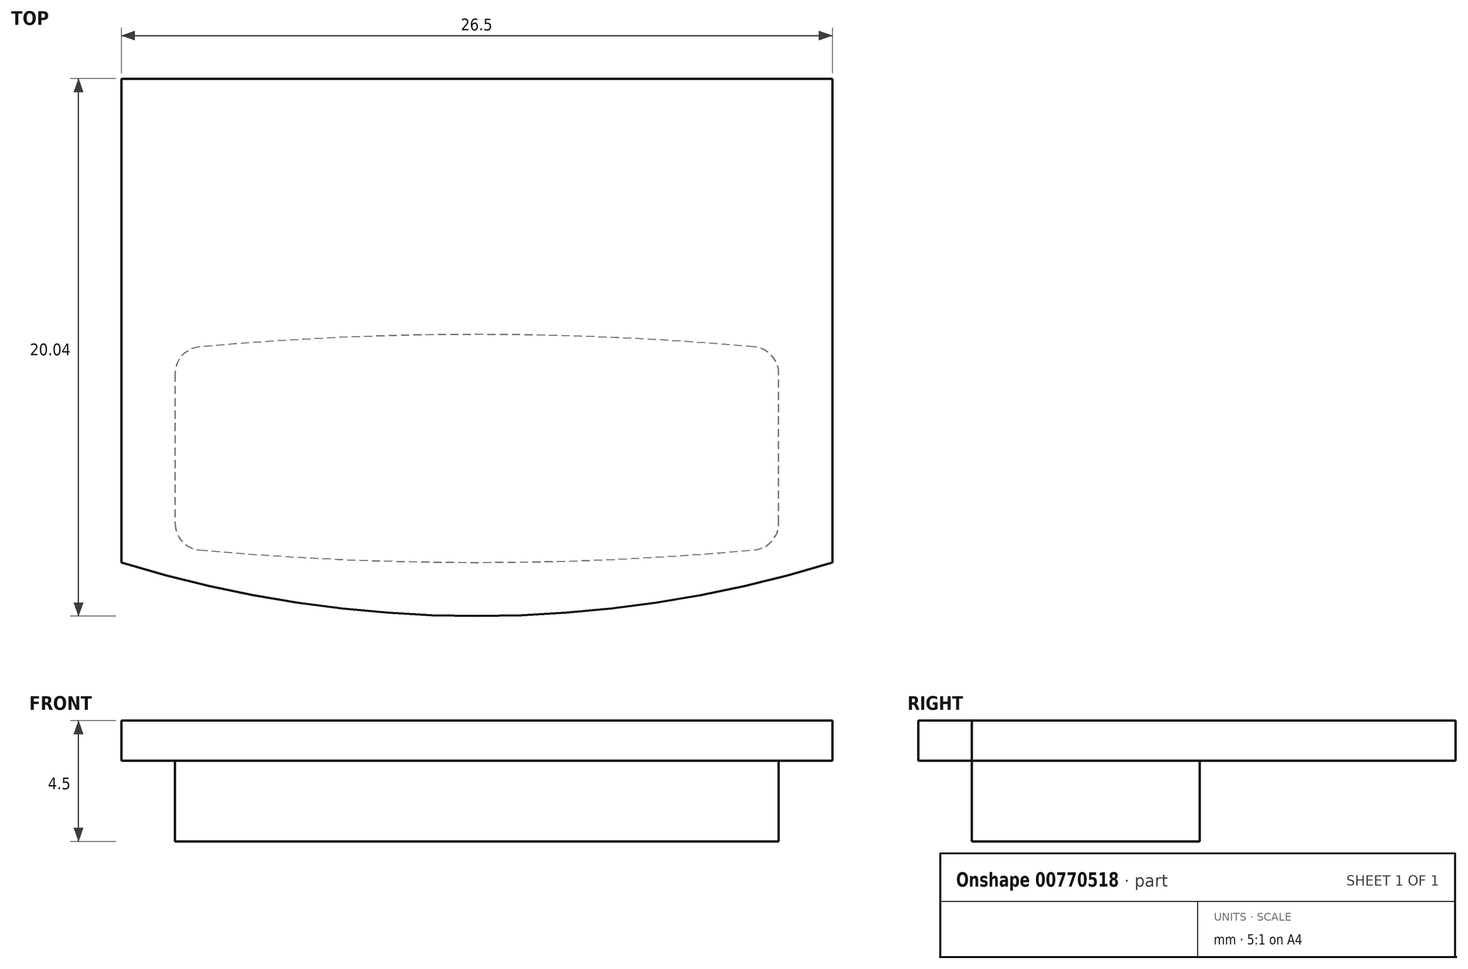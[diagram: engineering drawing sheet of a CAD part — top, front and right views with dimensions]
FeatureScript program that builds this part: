
annotation { "Feature Type Name" : "Feature", "Feature Type Description" : "" }
export const myFeature = defineFeature(function(context is Context, id is Id, definition is map)
    precondition{}
    {
        {
            var Q0;
            Q0=qCreatedBy(makeId("Top.planeOp"),FACE);
            var sketch = newSketch(context, id + "F0", { "sketchPlane" : qUnion([Q0])});
            skLineSegment(sketch, "E0.bottom", {"start": v(-21, 0) * mm, "end": v(0, 0) * mm, "construction": true});
            skLineSegment(sketch, "E0.top", {"start": v(-21, 7) * mm, "end": v(0, 7) * mm, "construction": true});
            skLineSegment(sketch, "E0.left", {"start": v(-21, 0) * mm, "end": v(-21, 7) * mm, "construction": true});
            skLineSegment(sketch, "E0.right", {"start": v(0, 0) * mm, "end": v(0, 7) * mm, "construction": true});
            skLineSegment(sketch, "E1", {"start": v(-10.5, 39.2) * mm, "end": v(-10.5, -34.84) * mm, "construction": true});
            skLineSegment(sketch, "E2", {"start": v(-38.92, 7.75) * mm, "end": v(29.36, 7.75) * mm, "construction": true});
            skLineSegment(sketch, "E3", {"start": v(-21.75, 7.2) * mm, "end": v(-21.75, -0.2) * mm});
            skLineSegment(sketch, "E4", {"start": v(0.75, -0.2) * mm, "end": v(0.75, 7.2) * mm});
            skArc(sketch, "E5", {"start": v(0.75, 7.2) * mm, "mid": v(-10.5, 7.75) * mm, "end": v(-21.75, 7.2) * mm});
            skLineSegment(sketch, "E6", {"start": v(-32.96, -0.75) * mm, "end": v(7.2, -0.75) * mm, "construction": true});
            skArc(sketch, "E7", {"start": v(-21.75, -0.2) * mm, "mid": v(-10.5, -0.75) * mm, "end": v(0.75, -0.2) * mm});
            skSolve(sketch);
        }
        {
            var Q0;
            Q0=qSketchRegion(id+"F0",true);
            extrude(context, id + "F1", {"entities" : qUnion([Q0]), "depth" : 3 * mm, "offsetDistance" : 25 * mm});
        }
        {
            var Q0;
            Q0=makeQuery(id+"F1.opExtrude","SWEPT_EDGE",EDGE,{"disambiguationData":[OSD([sQuery(id+"F0.wireOp",EDGE,"E3"),sQuery(id+"F0.wireOp",EDGE,"E5")])]});
            var Q1;
            Q1=makeQuery(id+"F1.opExtrude","SWEPT_EDGE",EDGE,{"disambiguationData":[OSD([sQuery(id+"F0.wireOp",EDGE,"E3"),sQuery(id+"F0.wireOp",EDGE,"E7")])]});
            var Q2;
            Q2=makeQuery(id+"F1.opExtrude","SWEPT_EDGE",EDGE,{"disambiguationData":[OSD([sQuery(id+"F0.wireOp",EDGE,"E4"),sQuery(id+"F0.wireOp",EDGE,"E7")])]});
            var Q3;
            Q3=makeQuery(id+"F1.opExtrude","SWEPT_EDGE",EDGE,{"disambiguationData":[OSD([sQuery(id+"F0.wireOp",EDGE,"E4"),sQuery(id+"F0.wireOp",EDGE,"E5")])]});
            fillet(context, id + "F2", {"entities" : qUnion([Q0, Q1, Q2, Q3]), "radius" : 1 * mm, "tangentPropagation" : true, "allowEdgeOverflow" : false});
        }
        {
            var Q0;
            Q0=makeQuery(id+"F1.opExtrude","CAP_FACE",FACE,{"disambiguationData":[OSD([sQuery(id+"F0.wireOp",EDGE,"E3"),sQuery(id+"F0.wireOp",EDGE,"E4"),sQuery(id+"F0.wireOp",EDGE,"E5"),sQuery(id+"F0.wireOp",EDGE,"E7")])],"isStart":false});
            var sketch = newSketch(context, id + "F3", { "sketchPlane" : qUnion([Q0])});
            skLineSegment(sketch, "E8.bottom", {"start": v(-23.75, -0.75) * mm, "end": v(2.75, -0.75) * mm, "construction": true});
            skLineSegment(sketch, "E8.top", {"start": v(-23.75, 17.29) * mm, "end": v(2.75, 17.29) * mm});
            skLineSegment(sketch, "E8.left", {"start": v(-23.75, -0.75) * mm, "end": v(-23.75, 17.29) * mm});
            skLineSegment(sketch, "E8.right", {"start": v(2.75, -0.75) * mm, "end": v(2.75, 17.29) * mm});
            skArc(sketch, "E9", {"start": v(-23.75, -0.75) * mm, "mid": v(-10.5, -2.75) * mm, "end": v(2.75, -0.75) * mm});
            skLineSegment(sketch, "E10", {"start": v(-33.47, -2.75) * mm, "end": v(16.76, -2.75) * mm, "construction": true});
            skSolve(sketch);
        }
        {
            var Q0;
            Q0=qSketchRegion(id+"F3",true);
            extrude(context, id + "F4", {"entities" : qUnion([Q0]), "operationType" : NewBodyOperationType.ADD, "depth" : 1.5 * mm, "offsetDistance" : 25 * mm});
        }
    });
